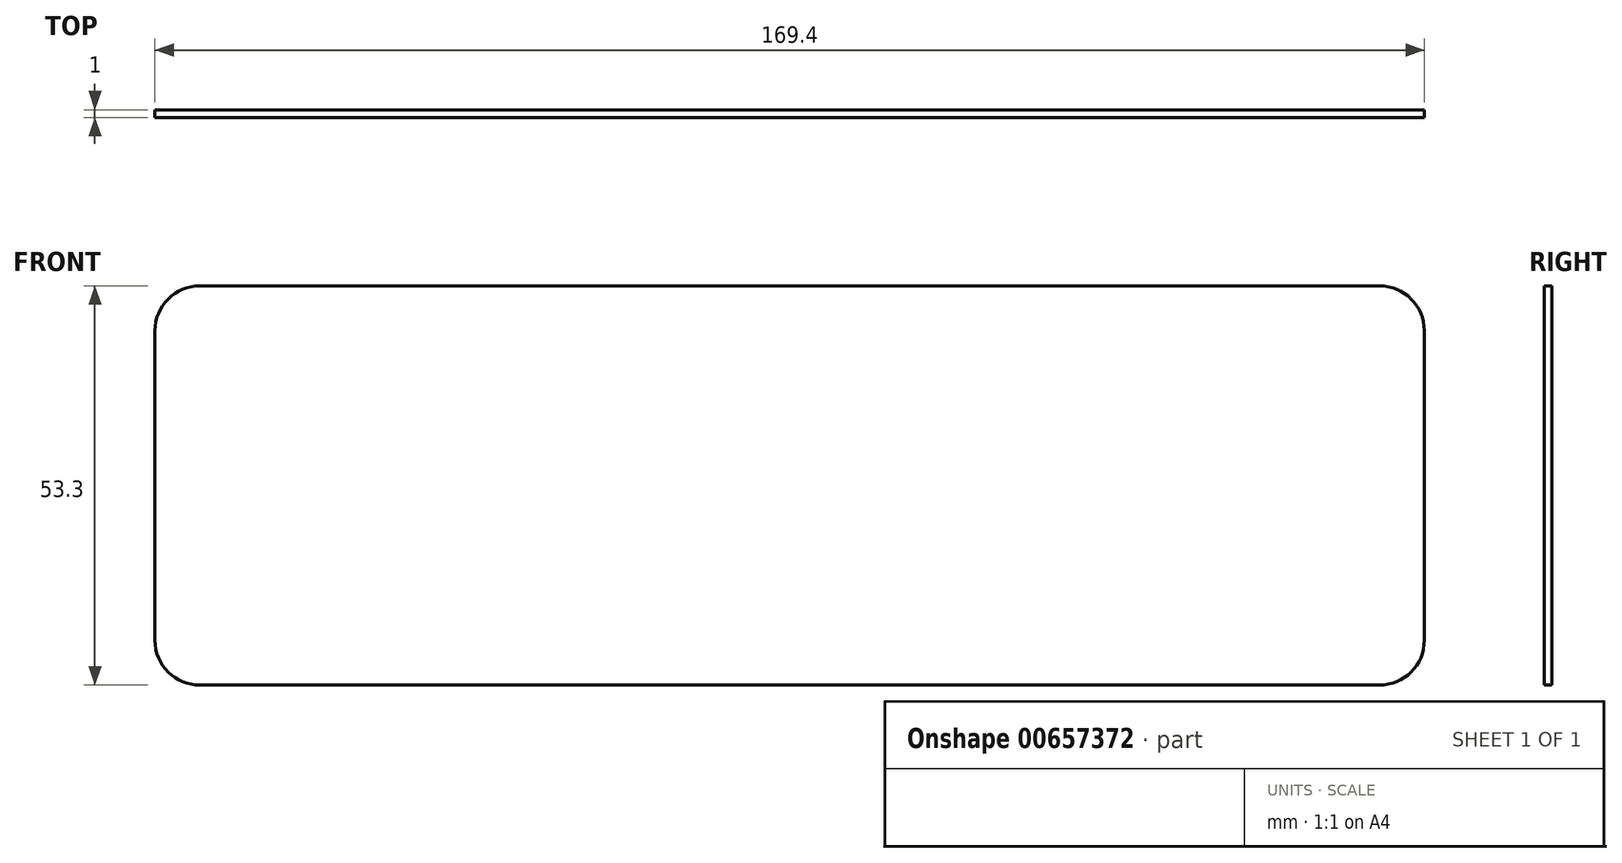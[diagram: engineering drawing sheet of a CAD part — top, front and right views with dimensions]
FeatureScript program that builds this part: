
annotation { "Feature Type Name" : "Feature", "Feature Type Description" : "" }
export const myFeature = defineFeature(function(context is Context, id is Id, definition is map)
    precondition{}
    {
        {
            var Q0;
            Q0=qCreatedBy(makeId("Front.planeOp"),FACE);
            var sketch = newSketch(context, id + "F0", { "sketchPlane" : qUnion([Q0])});
            skLineSegment(sketch, "E0", {"start": v(-108.51, -23.45) * mm, "end": v(48.89, -23.45) * mm});
            skLineSegment(sketch, "E1", {"start": v(48.89, 29.85) * mm, "end": v(-108.51, 29.85) * mm});
            skArc(sketch, "E2", {"start": v(-114.51, -17.45) * mm, "mid": v(-112.76, -21.7) * mm, "end": v(-108.51, -23.45) * mm});
            skLineSegment(sketch, "E3", {"start": v(54.89, -17.45) * mm, "end": v(54.89, 23.85) * mm});
            skArc(sketch, "E4", {"start": v(48.89, -23.45) * mm, "mid": v(53.13, -21.7) * mm, "end": v(54.89, -17.45) * mm});
            skArc(sketch, "E5", {"start": v(54.89, 23.85) * mm, "mid": v(53.13, 28.1) * mm, "end": v(48.89, 29.85) * mm});
            skLineSegment(sketch, "E6", {"start": v(-114.51, 23.85) * mm, "end": v(-114.51, -17.45) * mm});
            skArc(sketch, "E7", {"start": v(-108.51, 29.85) * mm, "mid": v(-112.76, 28.1) * mm, "end": v(-114.51, 23.85) * mm});
            skSolve(sketch);
        }
        {
            var Q0;
            Q0=makeQuery(id+"F0.imprint","IMPRINT",FACE,{"disambiguationData":[TD([[makeQuery(id+"F0.imprint","IMPRINT",EDGE,{"derivedFrom":sQuery(id+"F0.wireOp",EDGE,"E0")}),1.0]])]});
            extrude(context, id + "F1", {"entities" : qUnion([Q0]), "depth" : 1 * mm, "offsetDistance" : 25 * mm});
        }
    });
